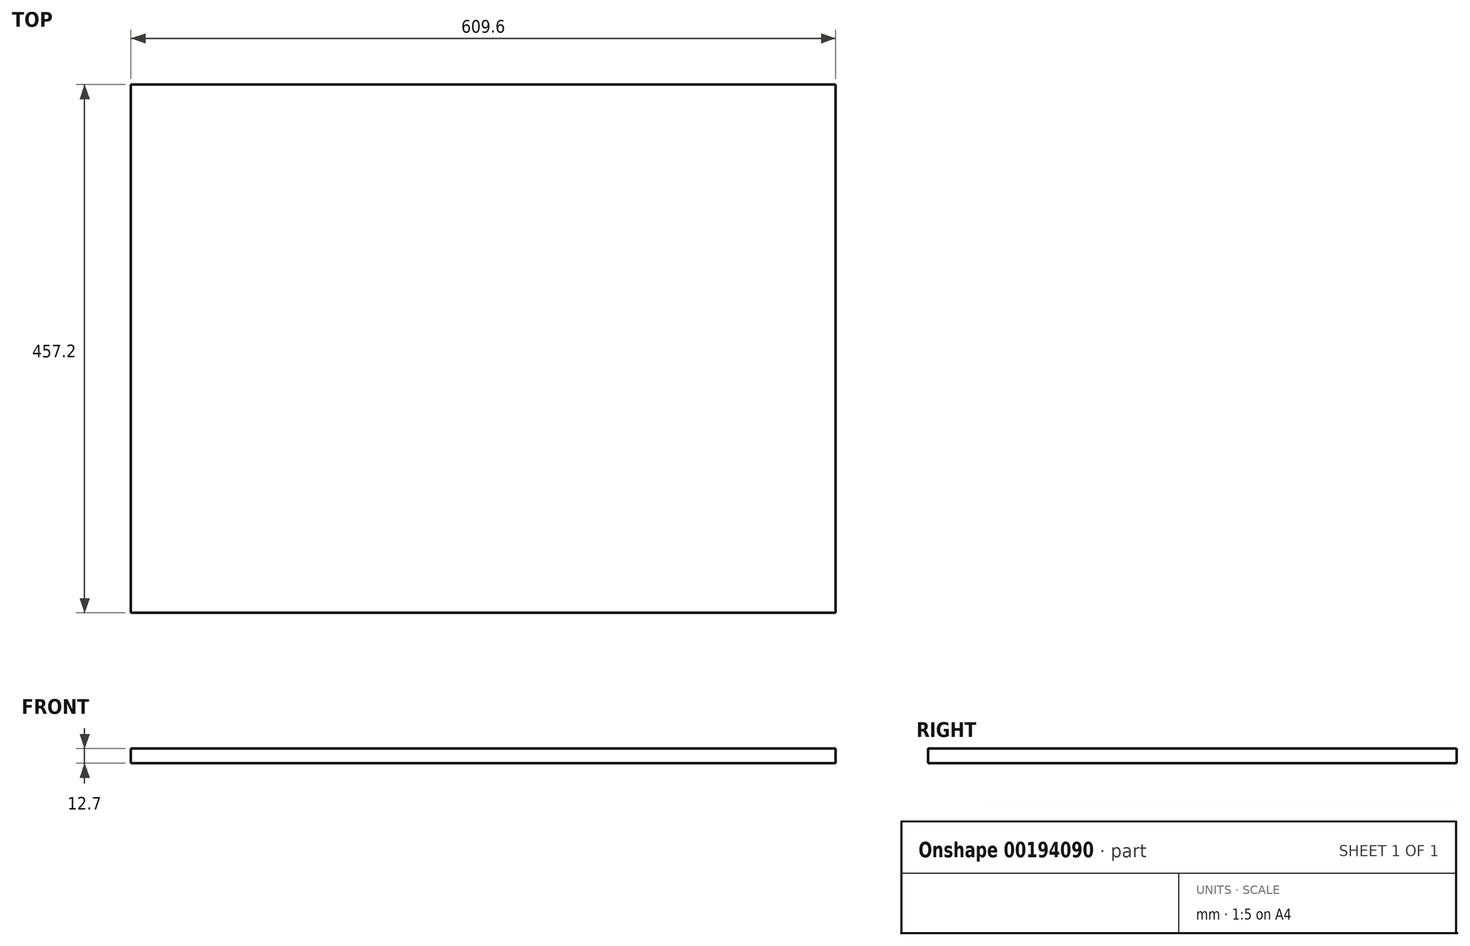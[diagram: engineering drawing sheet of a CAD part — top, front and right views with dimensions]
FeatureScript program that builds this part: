
annotation { "Feature Type Name" : "Feature", "Feature Type Description" : "" }
export const myFeature = defineFeature(function(context is Context, id is Id, definition is map)
    precondition{}
    {
        {
            var Q0;
            Q0=qCreatedBy(makeId("Top.planeOp"),FACE);
            var sketch = newSketch(context, id + "F0", { "sketchPlane" : qUnion([Q0])});
            skLineSegment(sketch, "E0.bottom", {"start": v(-489.5, 386.94) * mm, "end": v(120.1, 386.94) * mm});
            skLineSegment(sketch, "E0.top", {"start": v(-489.5, -70.26) * mm, "end": v(120.1, -70.26) * mm});
            skLineSegment(sketch, "E0.left", {"start": v(-489.5, 386.94) * mm, "end": v(-489.5, -70.26) * mm});
            skLineSegment(sketch, "E0.right", {"start": v(120.1, 386.94) * mm, "end": v(120.1, -70.26) * mm});
            skSolve(sketch);
        }
        {
            var Q0;
            Q0=makeQuery(id+"F0.imprint","IMPRINT",FACE,{"disambiguationData":[TD([[makeQuery(id+"F0.imprint","IMPRINT",EDGE,{"derivedFrom":sQuery(id+"F0.wireOp",EDGE,"E0.bottom")}),-1.0]])]});
            extrude(context, id + "F1", {"entities" : qUnion([Q0]), "depth" : 12.7 * mm});
        }
    });
